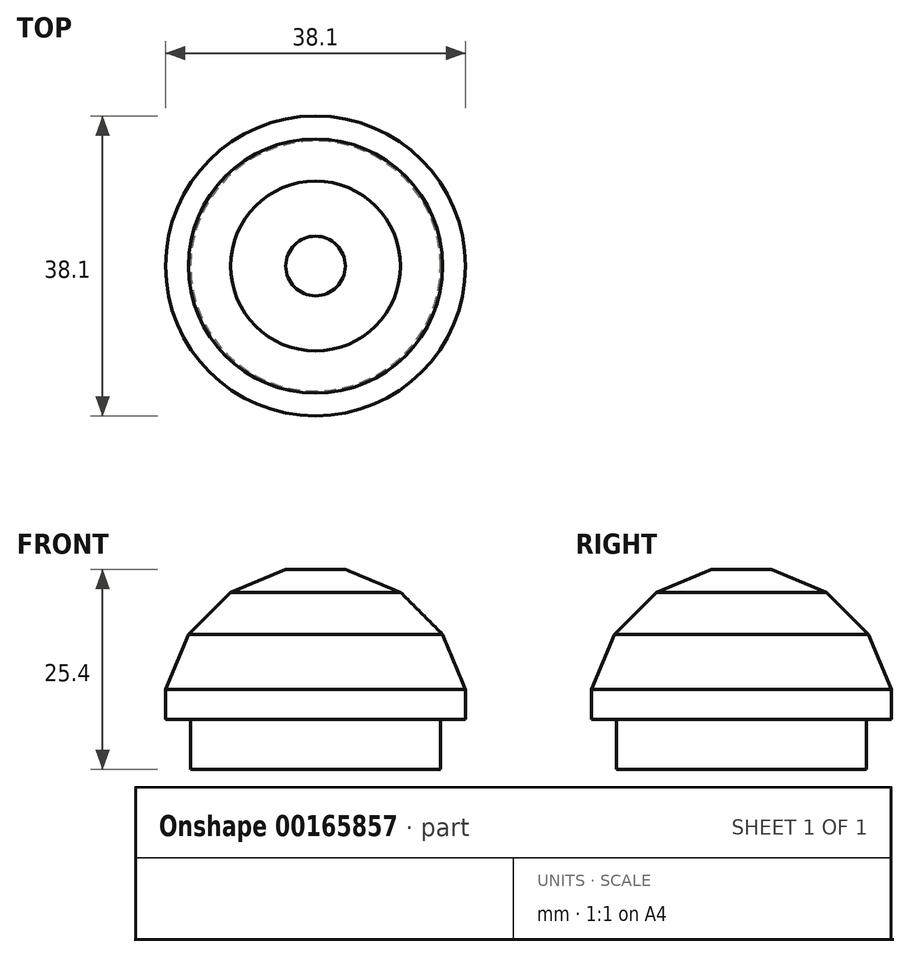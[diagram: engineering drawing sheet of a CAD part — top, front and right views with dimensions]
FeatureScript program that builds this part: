
annotation { "Feature Type Name" : "Feature", "Feature Type Description" : "" }
export const myFeature = defineFeature(function(context is Context, id is Id, definition is map)
    precondition{}
    {
        {
            var Q0;
            Q0=qCreatedBy(makeId("Front.planeOp"),FACE);
            var sketch = newSketch(context, id + "F0", { "sketchPlane" : qUnion([Q0])});
            skLineSegment(sketch, "E0", {"start": v(0, 0) * mm, "end": v(-15.88, 0) * mm});
            skLineSegment(sketch, "E1", {"start": v(-15.88, 0) * mm, "end": v(-15.88, 6.35) * mm});
            skLineSegment(sketch, "E2", {"start": v(-15.88, 6.35) * mm, "end": v(-19.05, 6.35) * mm});
            skLineSegment(sketch, "E3", {"start": v(-19.05, 6.35) * mm, "end": v(-19.05, 10.14) * mm});
            skLineSegment(sketch, "E4", {"start": v(-19.05, 10.14) * mm, "end": v(-16.15, 17.14) * mm});
            skLineSegment(sketch, "E5", {"start": v(-16.15, 17.14) * mm, "end": v(-10.8, 22.5) * mm});
            skLineSegment(sketch, "E6", {"start": v(-10.8, 22.5) * mm, "end": v(-3.79, 25.4) * mm});
            skLineSegment(sketch, "E7", {"start": v(-3.79, 25.4) * mm, "end": v(0, 25.4) * mm});
            skLineSegment(sketch, "E8", {"start": v(0, 25.4) * mm, "end": v(0, 0) * mm});
            skLineSegment(sketch, "E9", {"start": v(-3.79, 25.4) * mm, "end": v(3.79, 25.4) * mm, "construction": true});
            skSolve(sketch);
        }
        {
            var Q0;
            Q0=makeQuery(id+"F0.imprint","IMPRINT",FACE,{"disambiguationData":[TD([[makeQuery(id+"F0.imprint","IMPRINT",EDGE,{"derivedFrom":sQuery(id+"F0.wireOp",EDGE,"E0")}),-1.0]])]});
            var Q1;
            Q1=sQuery(id+"F0.wireOp",EDGE,"E8");
            revolve(context, id + "F1", {"entities" : qUnion([Q0]), "axis" : qUnion([Q1]), "revolveType" : RevolveType.FULL});
        }
    });
